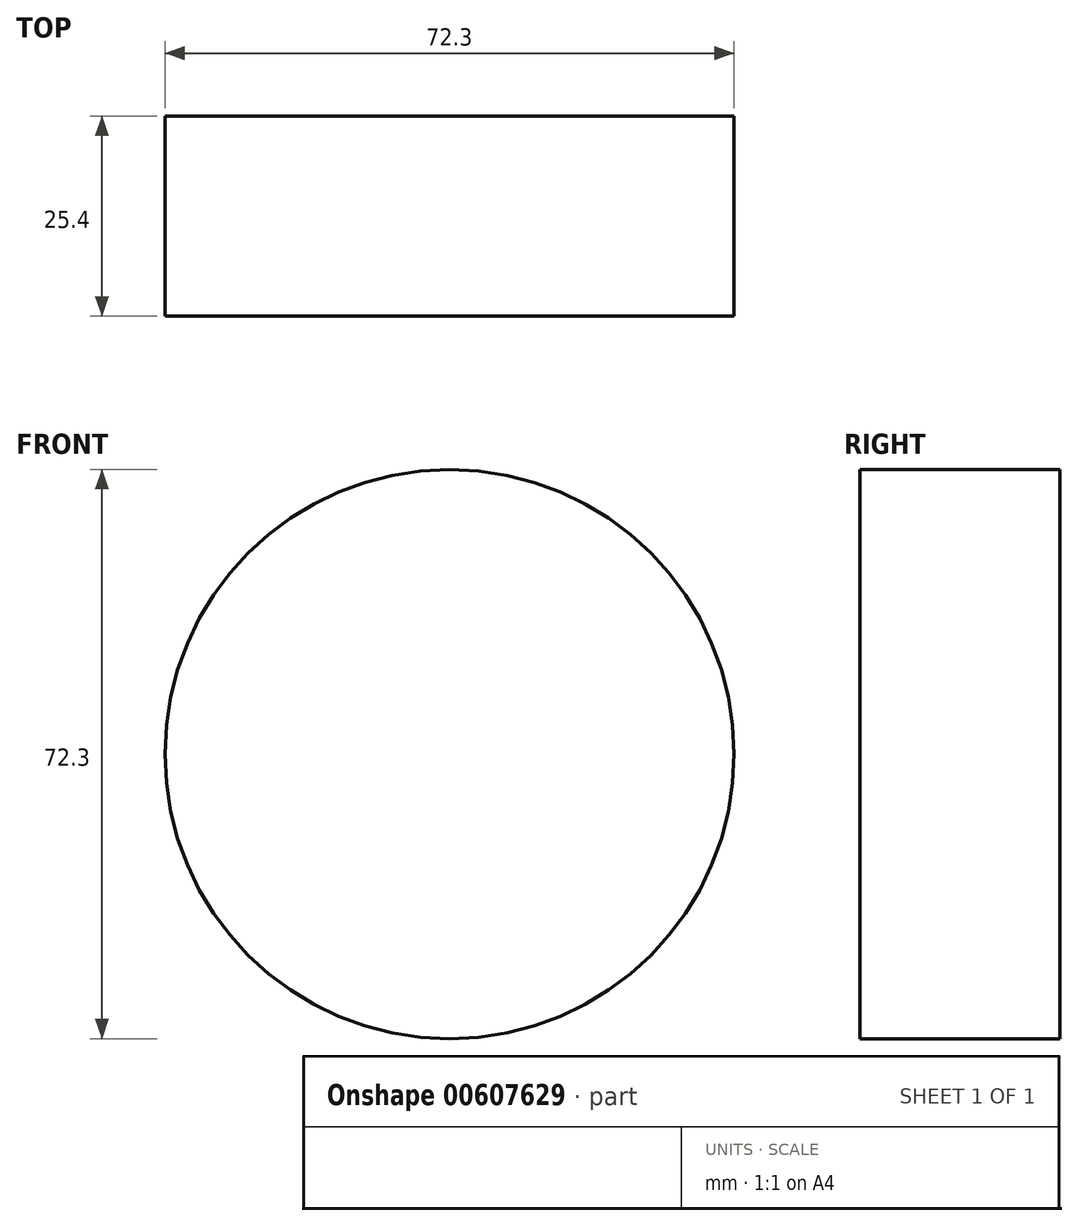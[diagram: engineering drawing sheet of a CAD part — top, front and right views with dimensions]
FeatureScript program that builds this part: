
annotation { "Feature Type Name" : "Feature", "Feature Type Description" : "" }
export const myFeature = defineFeature(function(context is Context, id is Id, definition is map)
    precondition{}
    {
        {
            var Q0;
            Q0=qCreatedBy(makeId("Front.planeOp"),FACE);
            var sketch = newSketch(context, id + "F0", { "sketchPlane" : qUnion([Q0])});
            skCircle(sketch, "E0", {"center": v(0, 0) * mm, "radius": 36.15 * mm});
            skSolve(sketch);
        }
        {
            var Q0;
            Q0 = qSketchRegion(id + "F0", true);
            extrude(context, id + "F1", {"entities" : qUnion([Q0]), "endBound" : BoundingType.SYMMETRIC, "depth" : 25.4 * mm, "offsetDistance" : 25.4 * mm});
        }
    });
